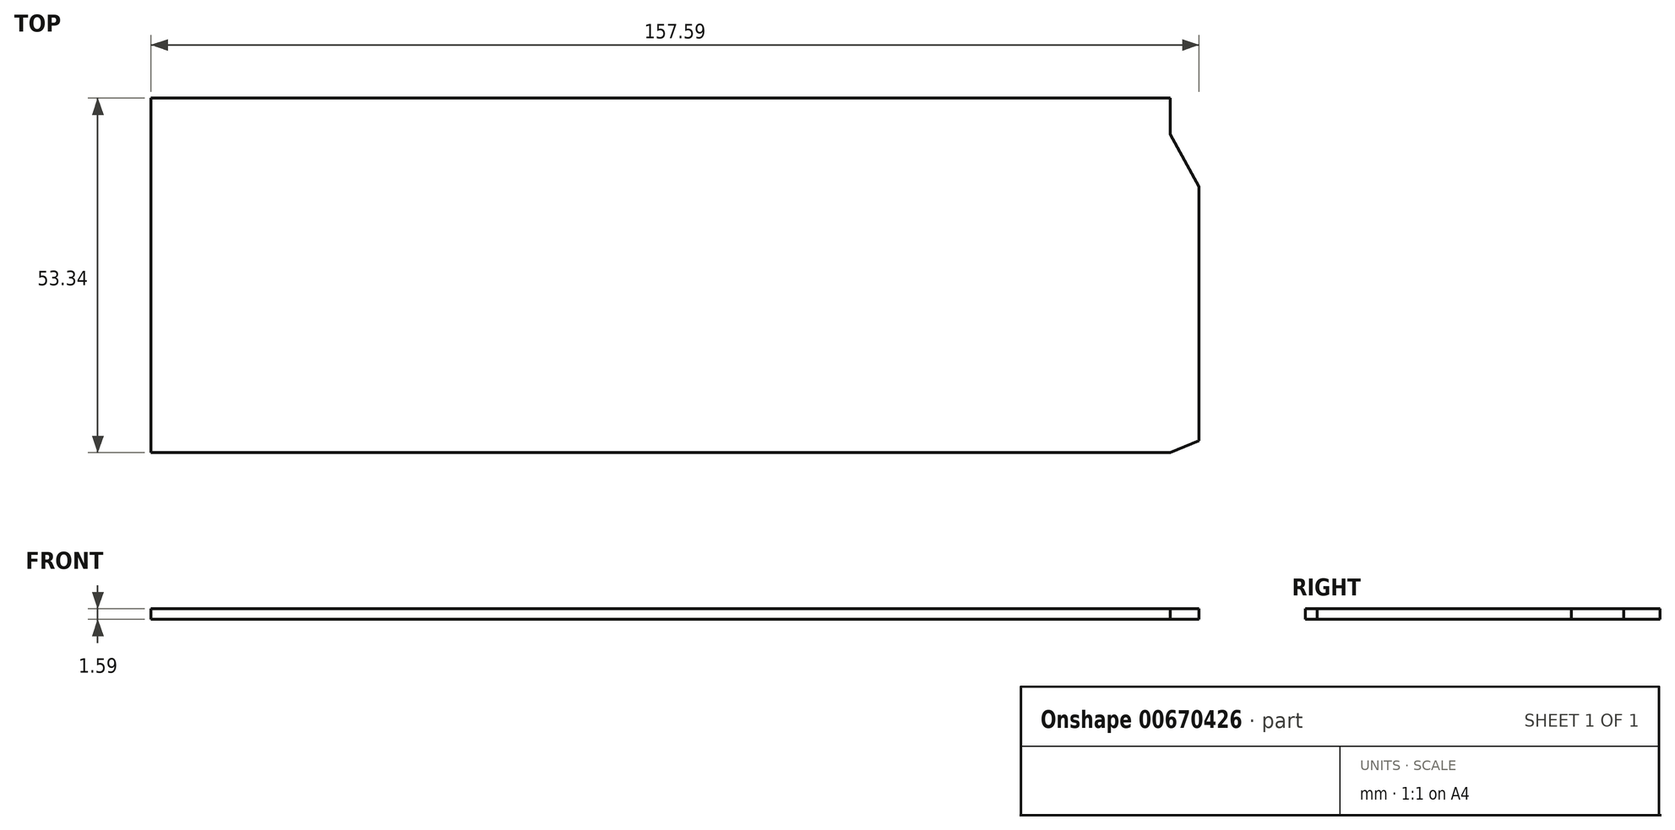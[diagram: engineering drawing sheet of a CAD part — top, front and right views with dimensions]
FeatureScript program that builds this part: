
annotation { "Feature Type Name" : "Feature", "Feature Type Description" : "" }
export const myFeature = defineFeature(function(context is Context, id is Id, definition is map)
    precondition{}
    {
        {
            var Q0;
            Q0=qCreatedBy(makeId("Top.planeOp"),FACE);
            var sketch = newSketch(context, id + "F0", { "sketchPlane" : qUnion([Q0])});
            skLineSegment(sketch, "E0", {"start": v(-79.04, 5.45) * mm, "end": v(74.24, 5.45) * mm});
            skLineSegment(sketch, "E1", {"start": v(74.24, 5.45) * mm, "end": v(74.24, 0) * mm});
            skLineSegment(sketch, "E2", {"start": v(74.24, -47.9) * mm, "end": v(-79.04, -47.9) * mm});
            skLineSegment(sketch, "E3", {"start": v(-79.04, -47.9) * mm, "end": v(-79.04, 5.45) * mm});
            skLineSegment(sketch, "E4", {"start": v(78.55, -7.87) * mm, "end": v(78.55, -46.1) * mm});
            skLineSegment(sketch, "E5", {"start": v(78.55, -46.1) * mm, "end": v(74.24, -47.9) * mm});
            skLineSegment(sketch, "E6", {"start": v(78.55, -7.87) * mm, "end": v(74.24, 0) * mm});
            skLineSegment(sketch, "E7", {"start": v(0, -22.29) * mm, "end": v(0, 5.45) * mm, "construction": true});
            skSolve(sketch);
        }
        {
            var Q0;
            Q0=makeQuery(id+"F0.imprint","IMPRINT",FACE,{"disambiguationData":[TD([[makeQuery(id+"F0.imprint","IMPRINT",EDGE,{"derivedFrom":sQuery(id+"F0.wireOp",EDGE,"E0")}),-1.0]])]});
            extrude(context, id + "F1", {"entities" : qUnion([Q0]), "depth" : 1.59 * mm, "offsetDistance" : 25 * mm});
        }
    });
